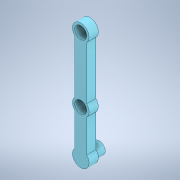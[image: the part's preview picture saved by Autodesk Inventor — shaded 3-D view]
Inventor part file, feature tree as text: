
AUTODESK INVENTOR PART (.ipt)
format: ipt  version: 2022 (Build 260153000, 153)  size: 141,312 bytes
history: native  units: in
note: dims shown in document units (in); Inventor stores cm internally (conversion verified against a paired STEP export)
features: extrude x2, sketch x1
ambient origin geometry x8: Origin, YZ Plane, XZ Plane, XY Plane, X Axis, Y Axis, Z Axis, Center Point
bodies: Solid1 (feature_tree)
feature tree (3):
  sketch  "Sketch2"  dims[d0=0.1969in d1=0.0in d2=0.1969in d3=0.0in d4=0.2559in d5=0.9449in d6=1.378in d8=0.3543in d9=0.2559in]
  extrude  "Extrusion1"  TaperAngle=0.0deg  [1 undecoded]
  extrude  "Extrusion2"  Depth=0.1969in TaperAngle=0.0deg
note: 1 required parameter value undecoded (feature->parameter linkage not recoverable at this tier; creation-order binding heuristic only, values carry confidence <= 0.55)
